# Revit family: Sanitary_Toilet-Accessories_DURAVIT-AG_Starck-T-Toilet-paper-holder-125x83x131ed
name_source: partatom
category: Generic Models
revit_build: Autodesk Revit 2018 (Build: 20190510_1515(x64)
units: mm (PartAtom-declared; Revit-internal decimal feet)

## family parameters
Can host rebar = No
Cut with Voids When Loaded = No
Host = Face
OmniClass Number = 23.31.19.19.17
OmniClass Title = Water Closet Seats
Part Type = Normal
Room Calculation Point = No
Round Connector Dimension = Use Diameter
Shared = No

## types (2) — shared parameters
BIMobject category = Toilet Accessories
Default Elevation = 1219 mm
Design country = Germany
ETIM classification = EC011196 | Toilet seat
Edition number = 1
IFC Classification = Furnishing Element
Installation instructions = https://duravit-public-assets.s3.eu-central-1.amazonaws.com
Manufacturer = Duravit
Manufacturer name = DURAVIT AG
Masterformat 2014 Code = 22 41 13.13
Masterformat 2014 Description = Residential Water Closets
Material main = Chrome
Model = Starck T Toilet paper holder 125x83x131 mm - 009940
OmniClass Code = 23-31 19 19 17
OmniClass Description = Water Closet Seats
Product Guid = d869e24e-1a3e-433d-aaf4-5fda50915ca2
Product SKU = Starck-T-Toilet-paper-holder-125x83x131-mm-009940
Product certification = http://pro.duravit.com
Product data url = https://bimobject.com
Product family = Starck T
Product group = Toilet paper holder
Product name = Starck T Toilet paper holder 125x83x131 mm - 009940
Product url = http://pro.duravit.com
QR code = https://bimobject.com
Technical description = http://pro.duravit.com
UNSPSC Code = 301815
URL = https://www.duravit.com
Uniclass 2015 Code = Pr_40_20_93_95
Uniclass 2015 Name = WC seats and covers
Uniformat II Code = E2010
Uniformat II Description = Fixed Furnishings
Weight Net (Kg) = 0,4
Youtube clip = http://pro.duravit.com

## per-type parameters (varying)
| type | Description | Main material |
| 10 - Chrome | Duravit Starck T Toilet paper holder Chrome 125x83x131 mm - 0099401000 | Duravit - Metal - 10 - Chrome |
| 46 - Black Matt | Duravit Starck T Toilet paper holder Black Matt 125x83x131 mm - 0099404600 | Duravit - Metal - 46 - Black Matt |

## geometry (parser evidence)
native form markers: Sweep x3
no freeform markers — native parametric forms only
